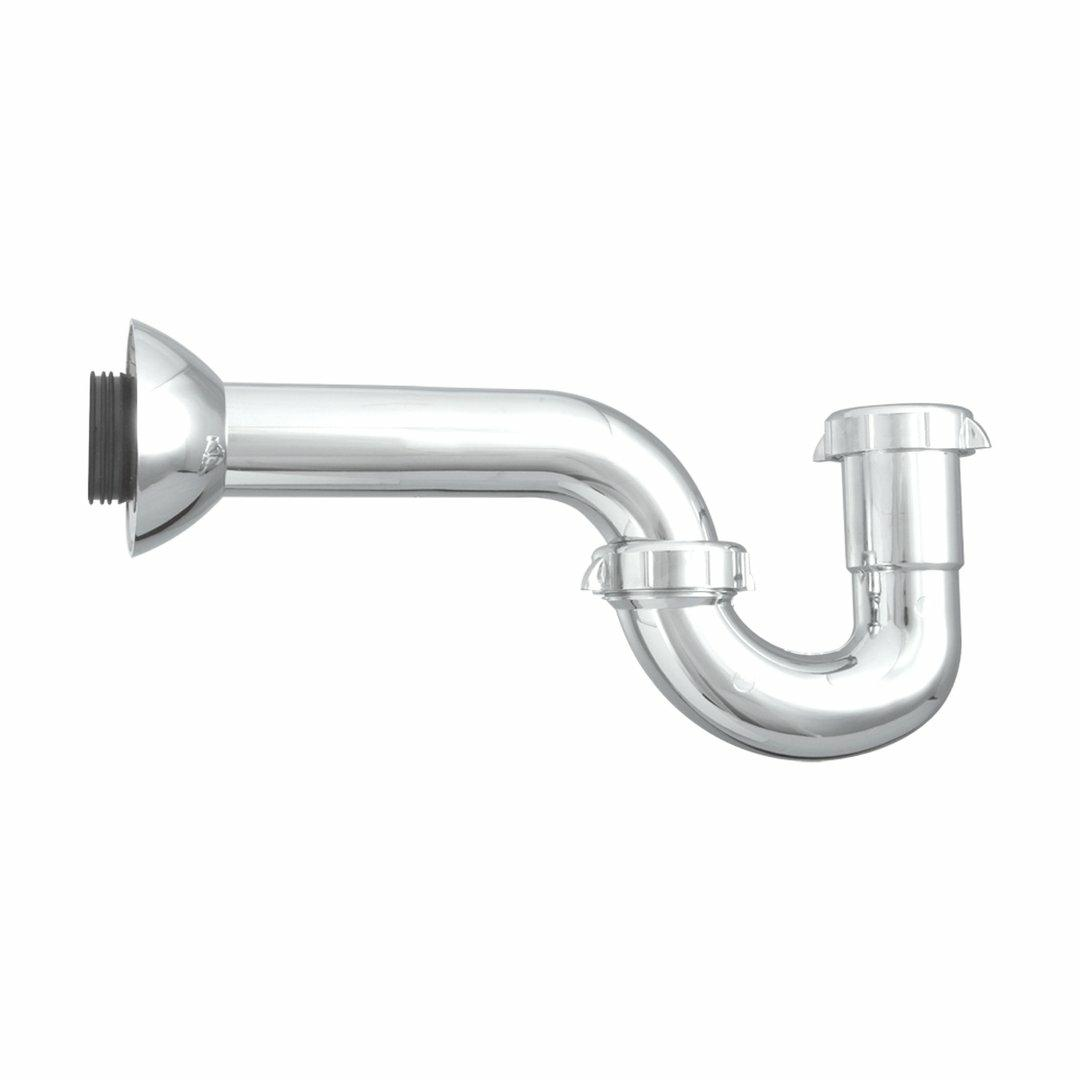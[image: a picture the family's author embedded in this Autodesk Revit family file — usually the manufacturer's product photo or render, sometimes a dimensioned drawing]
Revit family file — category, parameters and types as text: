
# Revit family: BIM_M1-3004-11
name_source: partatom
category: Aparatos sanitarios
units: mm (PartAtom-declared; Revit-internal decimal feet)

## family parameters
Activar corte en vistas = No
Anfitrión = Cara
Compartido = No
Corte con vacíos al cargar = No
Cota de conector redondo = Usar diámetro
Mantener orientación de anotación = No
Número OmniClass = 23.31.11.00
Punto de cálculo de habitación = No
Tipo de pieza = Normal

## types (1)
- M1-3004-11
    Acabado = Cepillado Brillante
    Alto = 160 mm  [stored 0.524934 ft]
    Ancho = 940 mm  [stored 3.08399 ft]
    Conexión AC = Sí
    Conexión AF = Sí
    Conexión de residuos = No
    Conexión de ventilación = No
    Date Modified = 08-08-2025
    Descripción = Lavaplatos en acero
    Elevación por defecto = 0 mm  [stored 0 ft]
    Fabricante = Gricol
    Garantia Especifica = 5 años
    Imagen de tipo = FOTO LAVAPLATOS EN ACERO POCETA IZQUIERDA 94 x 48 cm.jpg
    Largo = 480 mm  [stored 1.5748 ft]
    Link Ficha Tecnica = https://infotecnica.gricol.com
    Material = Acero inoxidable
    Materiales del producto = Acero Inoxidable
    Modelo = M1-3004-11
    Nota clave = Perforación para instalar grifería monomando
    Peso = 3.80 kg
    Product Name = Lavaplatos Poceta Izquierda 94 X 48 Cm Con Complementos
    Resistencia a Corrosión = Si
    Sitio web = https://www.gricol.com
    Tipo de Uso = Residencial
    URL = https://www.gricol.com

note: [stored X ft] marks values corroborated as IEEE doubles in the binary element streams (Revit-internal decimal feet)

## geometry (parser evidence)
native form markers: Blend x2, Sweep x15
no freeform markers — native parametric forms only
